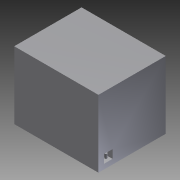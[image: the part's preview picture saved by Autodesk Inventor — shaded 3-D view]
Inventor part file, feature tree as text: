
AUTODESK INVENTOR PART (.ipt)
format: ipt  version: 2012 (Build 160160000, 160)  size: 111,616 bytes
history: native  units: in
note: dims shown in document units (in); Inventor stores cm internally (conversion verified against a paired STEP export)
features: extrude x5, sketch x5
ambient origin geometry x8: Origin, YZ Plane, XZ Plane, XY Plane, X Axis, Y Axis, Z Axis, Center Point
bodies: Solid1 (feature_tree)
feature tree (10):
  extrude  "Extrusion1"  Depth=8.0in
  extrude  "Extrusion3"  Depth=1.0in
  extrude  "Extrusion4"  Depth=0.6779in
  extrude  "Extrusion5"  Depth=1.0in TaperAngle=0.0deg
  extrude  "Extrusion6"  Depth=0.3in
  sketch  "Sketch1"  dims[d0=10.0in d1=8.0in]
  sketch  "Sketch3"  dims[d2=8.0in d3=0.0in d10=1.0in]
  sketch  "Sketch4"  dims[d11=1.0in d12=0.6779in]
  sketch  "Sketch5"  dims[d13=0.5799in d14=1.0in d15=0.0in]
  sketch  "Sketch6"  dims[d16=0.3in d17=0.3in d18=0.5in d19=0.0in d20=1.0in d21=1.0in d22=0.658in d23=0.58in d24=1.0in d25=0.0in d26=0.3in d27=0.3in d28=0.5in d29=0.0in]
